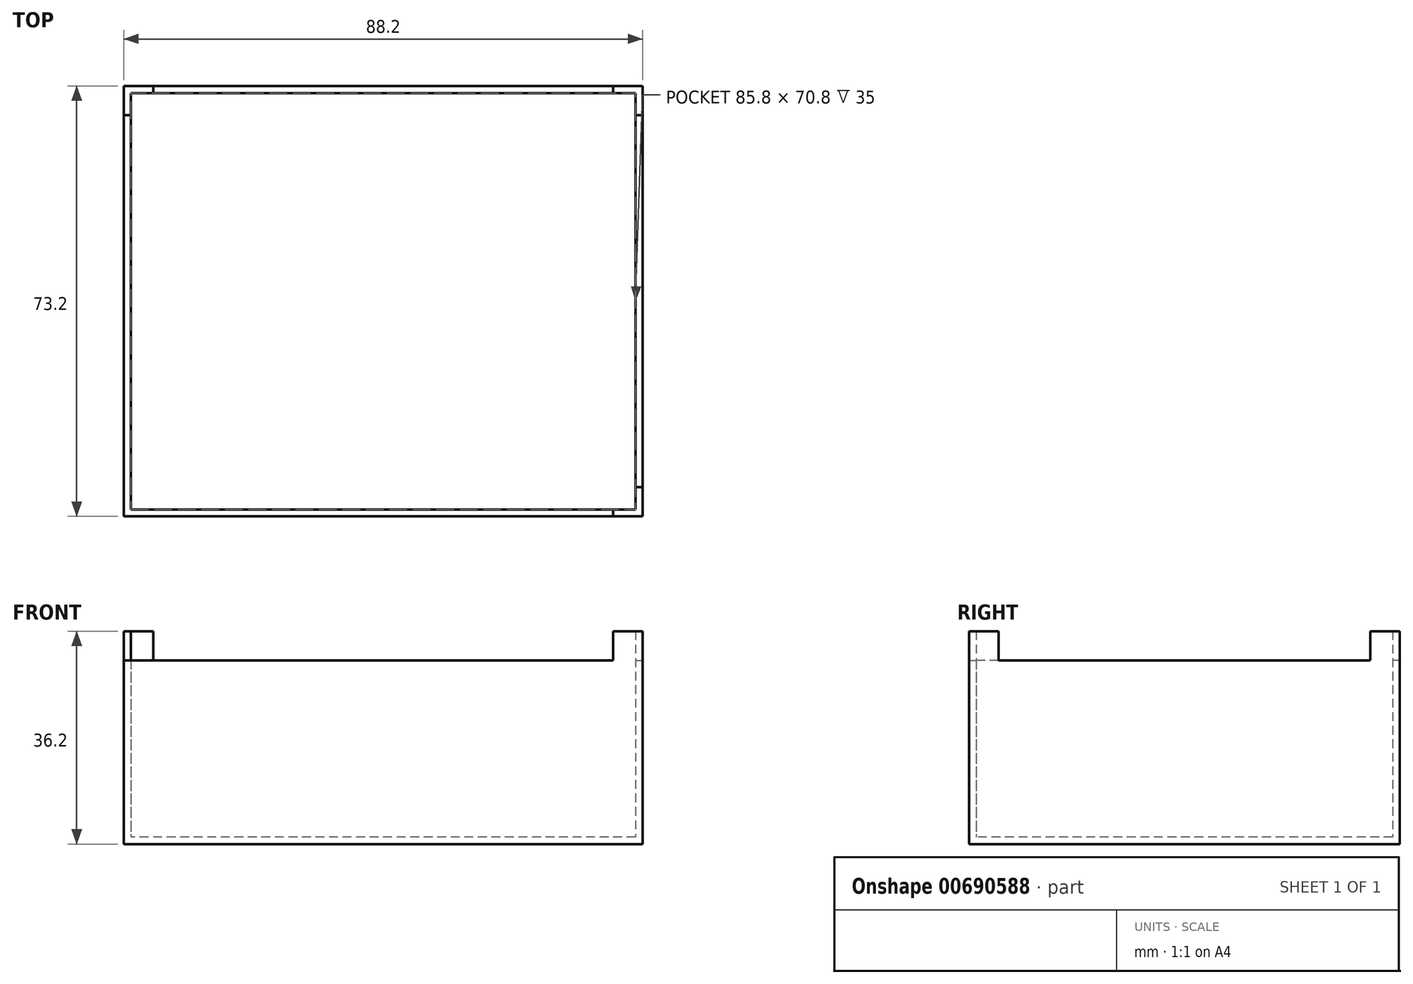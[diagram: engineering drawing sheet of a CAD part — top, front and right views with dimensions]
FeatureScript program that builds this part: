
annotation { "Feature Type Name" : "Feature", "Feature Type Description" : "" }
export const myFeature = defineFeature(function(context is Context, id is Id, definition is map)
    precondition{}
    {
        {
            var Q0;
            Q0=qCreatedBy(makeId("Top.planeOp"),FACE);
            var sketch = newSketch(context, id + "F0", { "sketchPlane" : qUnion([Q0])});
            skLineSegment(sketch, "E0.bottom", {"start": v(-44.1, 36.6) * mm, "end": v(44.1, 36.6) * mm});
            skLineSegment(sketch, "E0.top", {"start": v(-44.1, -36.6) * mm, "end": v(44.1, -36.6) * mm});
            skLineSegment(sketch, "E0.left", {"start": v(-44.1, 36.6) * mm, "end": v(-44.1, -36.6) * mm});
            skLineSegment(sketch, "E0.right", {"start": v(44.1, 36.6) * mm, "end": v(44.1, -36.6) * mm});
            skPoint(sketch, "E0.middle", {"position": v(0, 0) * mm});
            skSolve(sketch);
        }
        {
            var Q0;
            Q0=makeQuery(id+"F0.imprint","IMPRINT",FACE,{"disambiguationData":[TD([[makeQuery(id+"F0.imprint","IMPRINT",EDGE,{"derivedFrom":sQuery(id+"F0.wireOp",EDGE,"E0.bottom")}),-1.0]])]});
            extrude(context, id + "F1", {"entities" : qUnion([Q0]), "depth" : 1.2 * mm, "offsetDistance" : 25 * mm});
        }
        {
            var Q0;
            Q0=makeQuery(id+"F1.opExtrude","CAP_FACE",FACE,{"disambiguationData":[OSD([sQuery(id+"F0.wireOp",EDGE,"E0.bottom"),sQuery(id+"F0.wireOp",EDGE,"E0.top"),sQuery(id+"F0.wireOp",EDGE,"E0.left"),sQuery(id+"F0.wireOp",EDGE,"E0.right")])],"isStart":false});
            var sketch = newSketch(context, id + "F2", { "sketchPlane" : qUnion([Q0])});
            skLineSegment(sketch, "E1.0.0", {"start": v(-44.1, 36.6) * mm, "end": v(-44.1, -36.6) * mm});
            skLineSegment(sketch, "E1.0.1", {"start": v(-44.1, -36.6) * mm, "end": v(44.1, -36.6) * mm});
            skLineSegment(sketch, "E1.0.2", {"start": v(44.1, -36.6) * mm, "end": v(44.1, 36.6) * mm});
            skLineSegment(sketch, "E1.0.3", {"start": v(44.1, 36.6) * mm, "end": v(-44.1, 36.6) * mm});
            skLineSegment(sketch, "E2.0", {"start": v(-42.9, 35.4) * mm, "end": v(-42.9, -35.4) * mm});
            skLineSegment(sketch, "E2.1", {"start": v(42.9, 35.4) * mm, "end": v(-42.9, 35.4) * mm});
            skLineSegment(sketch, "E2.2", {"start": v(42.9, -35.4) * mm, "end": v(42.9, 35.4) * mm});
            skLineSegment(sketch, "E2.3", {"start": v(-42.9, -35.4) * mm, "end": v(42.9, -35.4) * mm});
            skSolve(sketch);
        }
        {
            var Q0;
            Q0 = qSketchRegion(id + "F2", true);
            extrude(context, id + "F3", {"entities" : qUnion([Q0]), "operationType" : NewBodyOperationType.ADD, "depth" : 30 * mm, "offsetDistance" : 25 * mm});
        }
        {
            var Q0;
            Q0=makeQuery(id+"F3.opExtrude","CAP_FACE",FACE,{"disambiguationData":[OSD([sQuery(id+"F2.wireOp",EDGE,"E1.0.0"),sQuery(id+"F2.wireOp",EDGE,"E1.0.1"),sQuery(id+"F2.wireOp",EDGE,"E1.0.2"),sQuery(id+"F2.wireOp",EDGE,"E1.0.3"),sQuery(id+"F2.wireOp",EDGE,"E2.0"),sQuery(id+"F2.wireOp",EDGE,"E2.1"),sQuery(id+"F2.wireOp",EDGE,"E2.2"),sQuery(id+"F2.wireOp",EDGE,"E2.3")])],"isStart":false});
            var sketch = newSketch(context, id + "F4", { "sketchPlane" : qUnion([Q0])});
            skLineSegment(sketch, "E3.bottom", {"start": v(44.1, -36.6) * mm, "end": v(39.1, -36.6) * mm});
            skLineSegment(sketch, "E3.top", {"start": v(42.9, -35.4) * mm, "end": v(39.1, -35.4) * mm});
            skLineSegment(sketch, "E3.left", {"start": v(44.1, -36.6) * mm, "end": v(44.1, -35.4) * mm});
            skLineSegment(sketch, "E3.right", {"start": v(39.1, -36.6) * mm, "end": v(39.1, -35.4) * mm});
            skLineSegment(sketch, "E4.top", {"start": v(42.9, -31.6) * mm, "end": v(44.1, -31.6) * mm});
            skLineSegment(sketch, "E4.left", {"start": v(42.9, -35.4) * mm, "end": v(42.9, -31.6) * mm});
            skLineSegment(sketch, "E4.right", {"start": v(44.1, -35.4) * mm, "end": v(44.1, -31.6) * mm});
            skLineSegment(sketch, "E5", {"start": v(0, -36.6) * mm, "end": v(0, 35.4) * mm, "construction": true});
            skLineSegment(sketch, "E6", {"start": v(-44.1, 0) * mm, "end": v(44.1, 0) * mm, "construction": true});
            skLineSegment(sketch, "E7.MirrorCS", {"start": v(42.9, 35.4) * mm, "end": v(42.9, 31.6) * mm});
            skLineSegment(sketch, "E8.MirrorCS", {"start": v(44.1, 35.4) * mm, "end": v(44.1, 31.6) * mm});
            skLineSegment(sketch, "E9.MirrorCS", {"start": v(42.9, 31.6) * mm, "end": v(44.1, 31.6) * mm});
            skLineSegment(sketch, "E10.MirrorCS", {"start": v(44.1, 36.6) * mm, "end": v(39.1, 36.6) * mm});
            skLineSegment(sketch, "E11.MirrorCS", {"start": v(39.1, 36.6) * mm, "end": v(39.1, 35.4) * mm});
            skLineSegment(sketch, "E12.MirrorCS", {"start": v(44.1, 36.6) * mm, "end": v(44.1, 35.4) * mm});
            skLineSegment(sketch, "E13.MirrorCS", {"start": v(-44.1, 36.6) * mm, "end": v(-44.1, 35.4) * mm});
            skLineSegment(sketch, "E14.MirrorCS", {"start": v(-42.9, 31.6) * mm, "end": v(-44.1, 31.6) * mm});
            skLineSegment(sketch, "E15.MirrorCS", {"start": v(-39.1, 36.6) * mm, "end": v(-39.1, 35.4) * mm});
            skLineSegment(sketch, "E16.MirrorCS", {"start": v(-44.1, 36.6) * mm, "end": v(-39.1, 36.6) * mm});
            skLineSegment(sketch, "E17.MirrorCS", {"start": v(-44.1, 35.4) * mm, "end": v(-44.1, 31.6) * mm});
            skLineSegment(sketch, "E18.MirrorCS", {"start": v(-42.9, 35.4) * mm, "end": v(-42.9, 31.6) * mm});
            skSolve(sketch);
        }
        {
            var Q0;
            Q0 = qSketchRegion(id + "F4", true);
            var Q1;
            {var subQ0=sQuery(id+"F4.wireOp",EDGE,"E7.MirrorCS");Q1=makeQuery(id+"F4.imprint","IMPRINT",FACE,{"disambiguationData":[TD([[makeQuery(id+"F4.imprint","IMPRINT",EDGE,{"derivedFrom":subQ0}),-1.0]])]});}
            var Q2;
            Q2=makeQuery(id+"F4.imprint","IMPRINT",FACE,{"disambiguationData":[TD([[makeQuery(id+"F4.imprint","IMPRINT",EDGE,{"derivedFrom":sQuery(id+"F4.wireOp",EDGE,"E13.MirrorCS")}),1.0]])]});
            extrude(context, id + "F5", {"entities" : qUnion([Q0, Q1, Q2]), "operationType" : NewBodyOperationType.ADD, "depth" : 5 * mm, "offsetDistance" : 25 * mm});
        }
    });
